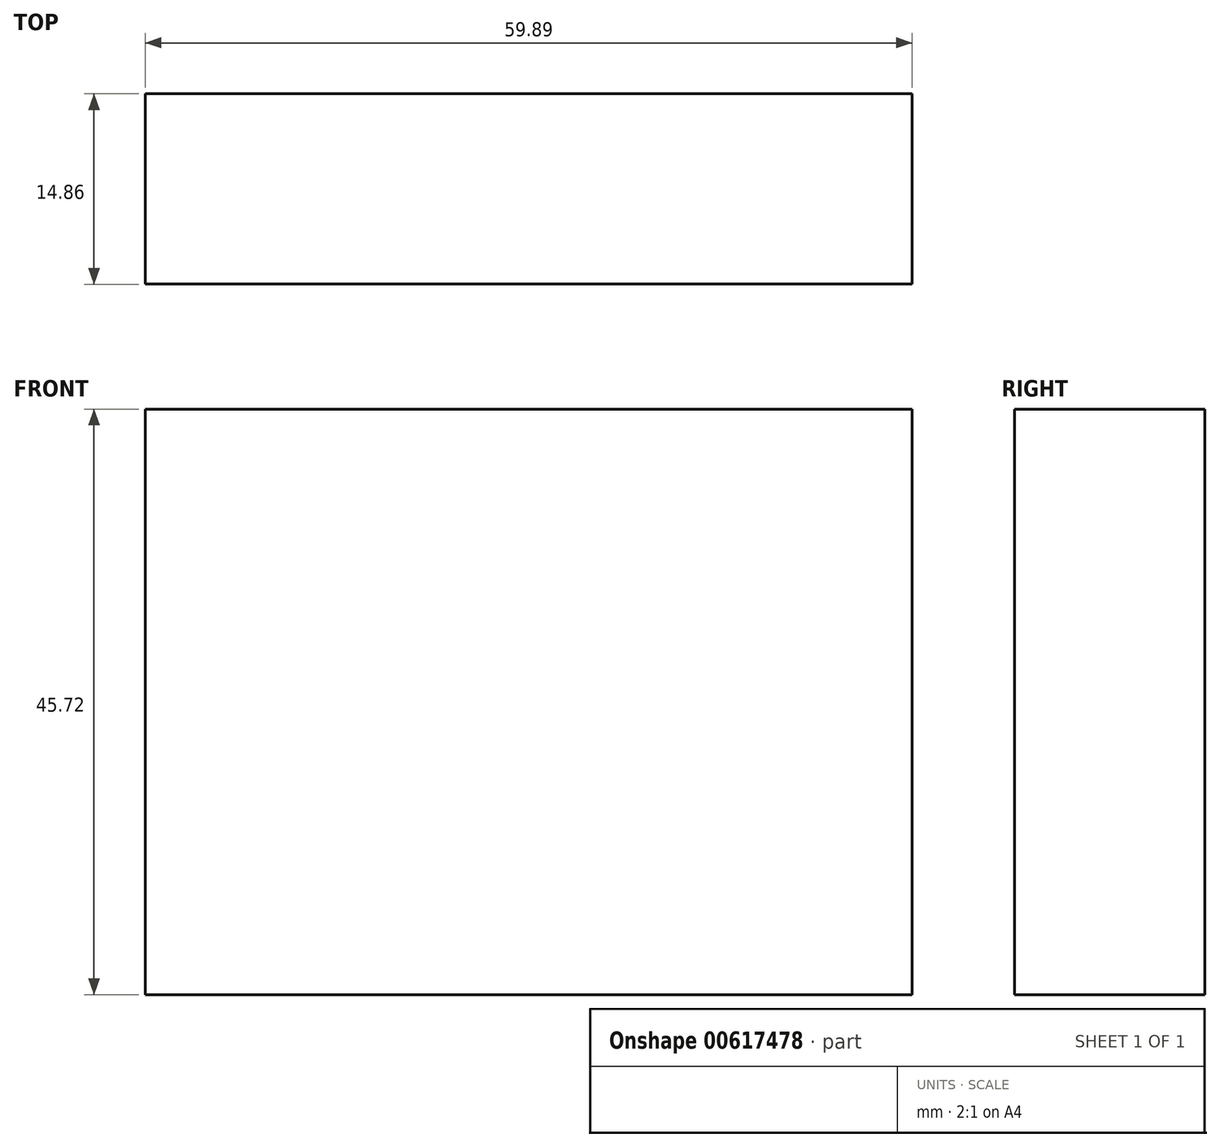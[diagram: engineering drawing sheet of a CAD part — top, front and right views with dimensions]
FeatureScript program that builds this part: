
annotation { "Feature Type Name" : "Feature", "Feature Type Description" : "" }
export const myFeature = defineFeature(function(context is Context, id is Id, definition is map)
    precondition{}
    {
        {
            var Q0;
            Q0=qCreatedBy(makeId("Front.planeOp"),FACE);
            var sketch = newSketch(context, id + "F0", { "sketchPlane" : qUnion([Q0])});
            skLineSegment(sketch, "E0", {"start": v(0, 0) * mm, "end": v(-59.9, 0) * mm});
            skLineSegment(sketch, "E1", {"start": v(-59.9, 0) * mm, "end": v(-59.9, 15.24) * mm});
            skLineSegment(sketch, "E2", {"start": v(-59.9, 15.24) * mm, "end": v(-59.9, 30.48) * mm});
            skLineSegment(sketch, "E3", {"start": v(-59.9, 30.48) * mm, "end": v(-59.9, 45.72) * mm});
            skLineSegment(sketch, "E4", {"start": v(-59.9, 45.72) * mm, "end": v(0, 45.72) * mm});
            skLineSegment(sketch, "E5", {"start": v(0, 45.72) * mm, "end": v(0, 0) * mm});
            skSolve(sketch);
        }
        {
            var Q0;
            Q0 = qSketchRegion(id + "F0", true);
            extrude(context, id + "F1", {"entities" : qUnion([Q0]), "depth" : 14.86 * mm, "offsetDistance" : 25.4 * mm});
        }
    });
